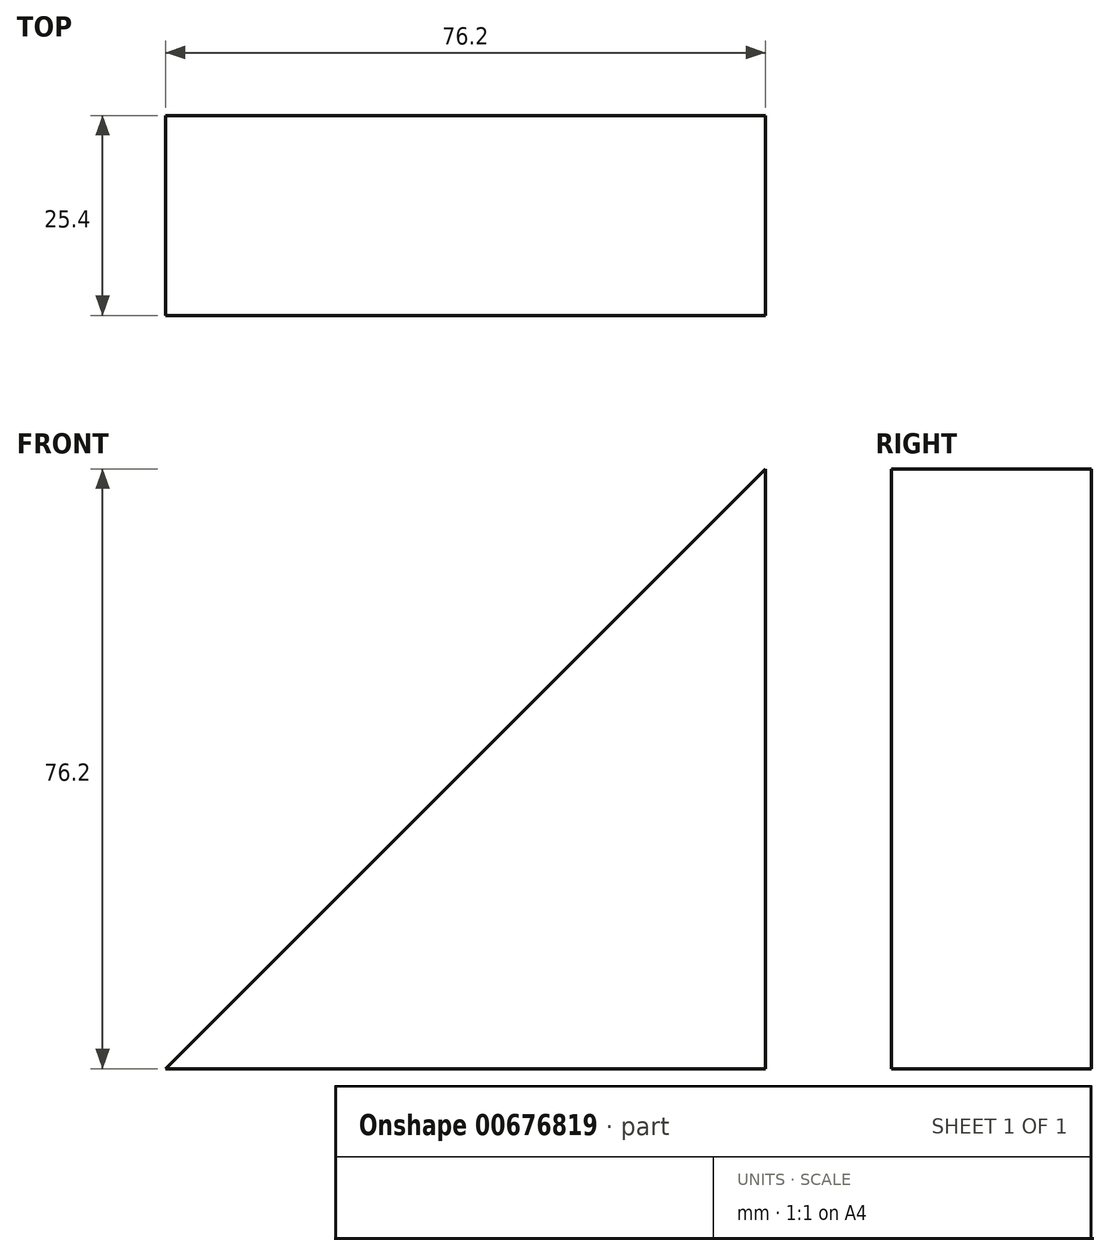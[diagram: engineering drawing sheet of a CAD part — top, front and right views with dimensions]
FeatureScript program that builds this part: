
annotation { "Feature Type Name" : "Feature", "Feature Type Description" : "" }
export const myFeature = defineFeature(function(context is Context, id is Id, definition is map)
    precondition{}
    {
        {
            var Q0;
            Q0=qCreatedBy(makeId("Front.planeOp"),FACE);
            var sketch = newSketch(context, id + "F0", { "sketchPlane" : qUnion([Q0])});
            skLineSegment(sketch, "E0", {"start": v(-76.2, 0) * mm, "end": v(0, 76.2) * mm});
            skLineSegment(sketch, "E1", {"start": v(0, 76.2) * mm, "end": v(0, 0) * mm});
            skLineSegment(sketch, "E2", {"start": v(0, 0) * mm, "end": v(-76.2, 0) * mm});
            skSolve(sketch);
        }
        {
            var Q0;
            Q0 = qSketchRegion(id + "F0", true);
            extrude(context, id + "F1", {"entities" : qUnion([Q0]), "depth" : 25.4 * mm, "offsetDistance" : 25.4 * mm});
        }
    });
